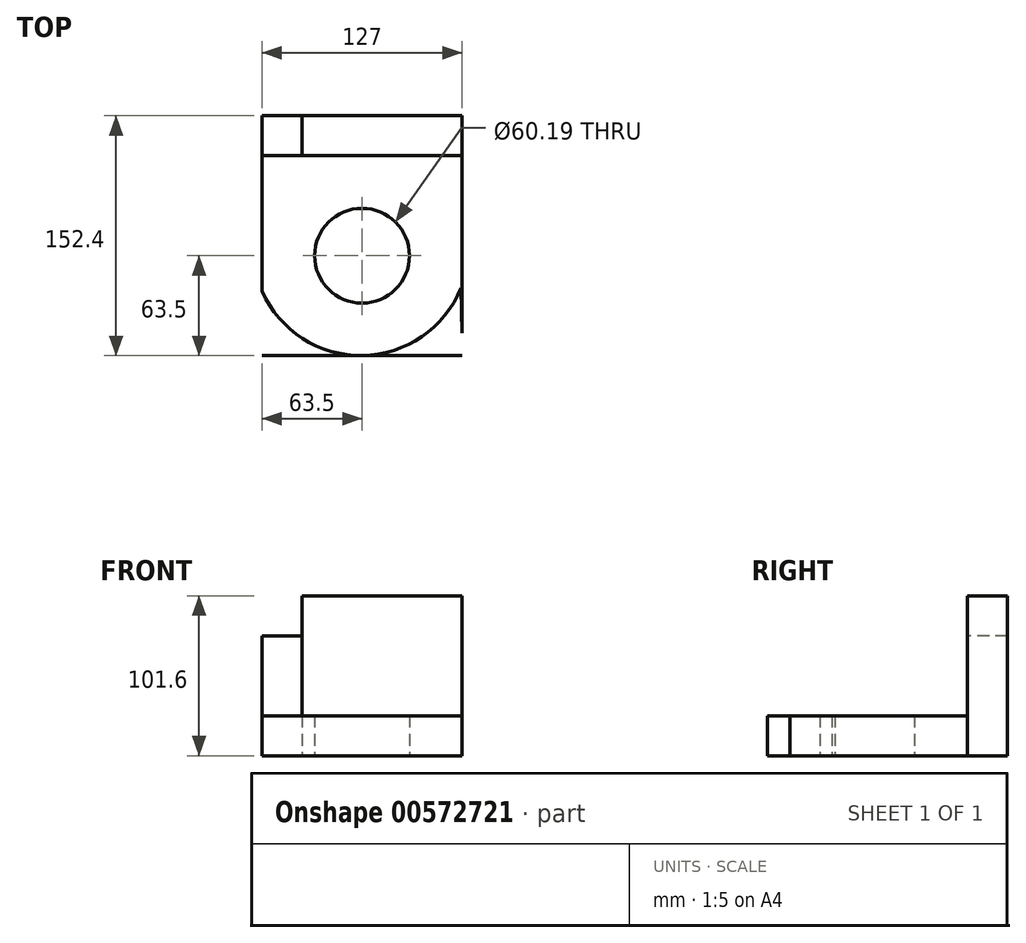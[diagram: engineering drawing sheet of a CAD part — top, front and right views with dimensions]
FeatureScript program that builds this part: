
annotation { "Feature Type Name" : "Feature", "Feature Type Description" : "" }
export const myFeature = defineFeature(function(context is Context, id is Id, definition is map)
    precondition{}
    {
        {
            var Q0;
            Q0=qCreatedBy(makeId("Top.planeOp"),FACE);
            var sketch = newSketch(context, id + "F0", { "sketchPlane" : qUnion([Q0])});
            skLineSegment(sketch, "E0.bottom", {"start": v(63.5, 63.5) * mm, "end": v(-63.5, 63.5) * mm});
            skLineSegment(sketch, "E0.top", {"start": v(63.5, -63.5) * mm, "end": v(-63.5, -63.5) * mm});
            skLineSegment(sketch, "E0.left", {"start": v(63.5, 63.5) * mm, "end": v(63.5, -63.5) * mm});
            skLineSegment(sketch, "E0.right", {"start": v(-63.5, 63.5) * mm, "end": v(-63.5, -63.5) * mm});
            skPoint(sketch, "E0.middle", {"position": v(0, 0) * mm});
            skSolve(sketch);
        }
        {
            var Q0;
            Q0=makeQuery(id+"F0.imprint","IMPRINT",FACE,{"disambiguationData":[TD([[makeQuery(id+"F0.imprint","IMPRINT",EDGE,{"derivedFrom":sQuery(id+"F0.wireOp",EDGE,"E0.bottom")}),1.0]])]});
            extrude(context, id + "F1", {"entities" : qUnion([Q0]), "depth" : 25.4 * mm, "offsetDistance" : 25.4 * mm});
        }
        {
            var Q0;
            Q0=qCreatedBy(makeId("Top.planeOp"),FACE);
            var sketch = newSketch(context, id + "F2", { "sketchPlane" : qUnion([Q0])});
            skCircle(sketch, "E1", {"center": v(0, 0) * mm, "radius": 30.1 * mm});
            skSolve(sketch);
        }
        {
            var Q0;
            Q0 = qSketchRegion(id + "F2", true);
            extrude(context, id + "F3", {"entities" : qUnion([Q0]), "operationType" : NewBodyOperationType.REMOVE, "depth" : 50.8 * mm, "offsetDistance" : 25.4 * mm});
        }
        {
            var Q0;
            Q0=qCreatedBy(makeId("Top.planeOp"),FACE);
            var sketch = newSketch(context, id + "F4", { "sketchPlane" : qUnion([Q0])});
            skArc(sketch, "E2", {"start": v(-63.86, -21.64) * mm, "mid": v(-0.18, -63.38) * mm, "end": v(62.8, -20.57) * mm});
            skLineSegment(sketch, "E3", {"start": v(-63.86, -21.64) * mm, "end": v(-63.86, -63.33) * mm});
            skLineSegment(sketch, "E4", {"start": v(-63.86, -63.33) * mm, "end": v(63.86, -63.44) * mm});
            skLineSegment(sketch, "E5", {"start": v(63.86, -63.44) * mm, "end": v(62.8, -20.57) * mm});
            skSolve(sketch);
        }
        {
            var Q0;
            Q0 = qSketchRegion(id + "F4", true);
            extrude(context, id + "F5", {"entities" : qUnion([Q0]), "operationType" : NewBodyOperationType.REMOVE, "depth" : 50.8 * mm, "offsetDistance" : 25.4 * mm});
        }
        {
            var Q0;
            Q0=qCreatedBy(makeId("Top.planeOp"),FACE);
            var sketch = newSketch(context, id + "F6", { "sketchPlane" : qUnion([Q0])});
            skLineSegment(sketch, "E6.bottom", {"start": v(-63.5, 88.9) * mm, "end": v(-38.1, 88.9) * mm});
            skLineSegment(sketch, "E6.top", {"start": v(-63.5, 63.5) * mm, "end": v(-38.1, 63.5) * mm});
            skLineSegment(sketch, "E6.left", {"start": v(-63.5, 88.9) * mm, "end": v(-63.5, 63.5) * mm});
            skLineSegment(sketch, "E6.right", {"start": v(-38.1, 88.9) * mm, "end": v(-38.1, 63.5) * mm});
            skSolve(sketch);
        }
        {
            var Q0;
            Q0=makeQuery(id+"F6.imprint","IMPRINT",FACE,{"disambiguationData":[TD([[makeQuery(id+"F6.imprint","IMPRINT",EDGE,{"derivedFrom":sQuery(id+"F6.wireOp",EDGE,"E6.bottom")}),-1.0]])]});
            extrude(context, id + "F7", {"entities" : qUnion([Q0]), "depth" : 76.2 * mm, "offsetDistance" : 25.4 * mm});
        }
        {
            var Q0;
            Q0=qCreatedBy(makeId("Top.planeOp"),FACE);
            var sketch = newSketch(context, id + "F8", { "sketchPlane" : qUnion([Q0])});
            skLineSegment(sketch, "E7.bottom", {"start": v(-38.1, 88.9) * mm, "end": v(63.5, 88.9) * mm});
            skLineSegment(sketch, "E7.top", {"start": v(-38.1, 63.5) * mm, "end": v(63.5, 63.5) * mm});
            skLineSegment(sketch, "E7.left", {"start": v(-38.1, 88.9) * mm, "end": v(-38.1, 63.5) * mm});
            skLineSegment(sketch, "E7.right", {"start": v(63.5, 88.9) * mm, "end": v(63.5, 63.5) * mm});
            skSolve(sketch);
        }
        {
            var Q0;
            Q0=makeQuery(id+"F8.imprint","IMPRINT",FACE,{"disambiguationData":[TD([[makeQuery(id+"F8.imprint","IMPRINT",EDGE,{"derivedFrom":sQuery(id+"F8.wireOp",EDGE,"E7.bottom")}),-1.0]])]});
            extrude(context, id + "F9", {"entities" : qUnion([Q0]), "depth" : 101.6 * mm, "offsetDistance" : 25.4 * mm});
        }
    });
